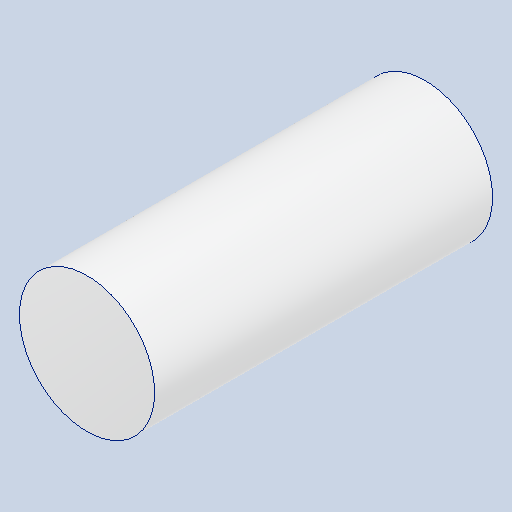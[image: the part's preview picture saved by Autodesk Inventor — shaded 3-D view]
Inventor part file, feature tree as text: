
AUTODESK INVENTOR PART (.ipt)
format: ipt  version: 2024 (Build 280153000, 153)  size: 196,608 bytes
history: native  units: mm
features: other x1, extrude x1, sketch x1
ambient origin geometry x8: Origin, YZ Plane, XZ Plane, XY Plane, X Axis, Y Axis, Z Axis, Center Point
bodies: Body1 (feature_tree)
feature tree (3):
  other  "솔리드1"
  extrude  "돌출1"  Depth=4.0mm
  sketch  "스케치1"
